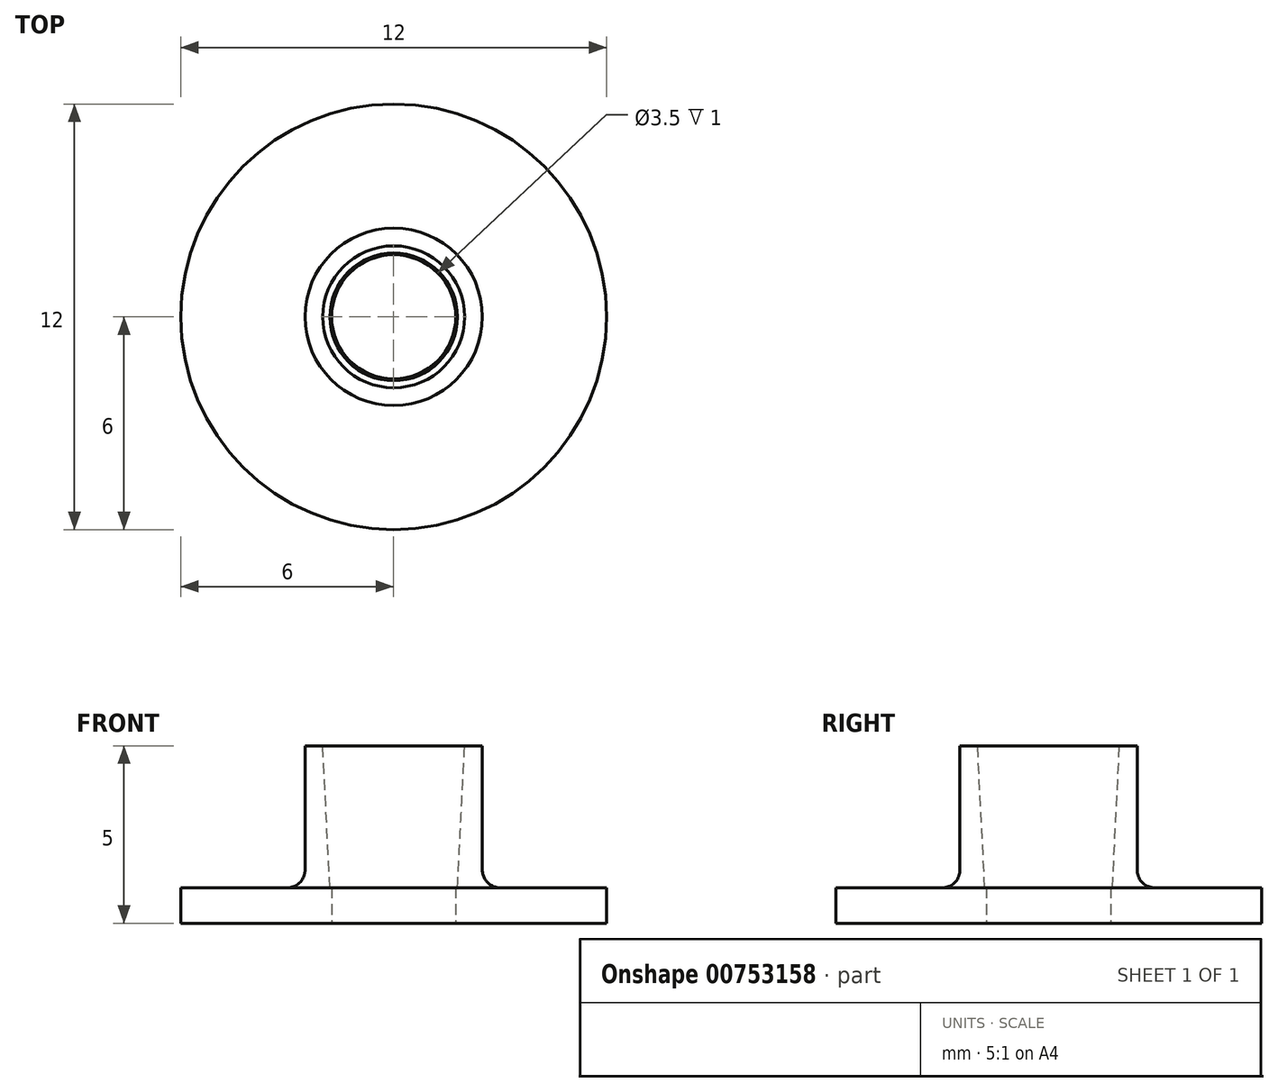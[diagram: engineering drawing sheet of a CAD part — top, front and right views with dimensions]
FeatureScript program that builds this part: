
annotation { "Feature Type Name" : "Feature", "Feature Type Description" : "" }
export const myFeature = defineFeature(function(context is Context, id is Id, definition is map)
    precondition{}
    {
        {
            var Q0;
            Q0=qCreatedBy(makeId("Top.planeOp"),FACE);
            var sketch = newSketch(context, id + "F0", { "sketchPlane" : qUnion([Q0])});
            skCircle(sketch, "E0", {"center": v(0, 0) * mm, "radius": 6 * mm});
            skCircle(sketch, "E1", {"center": v(0, 0) * mm, "radius": 1.75 * mm});
            skSolve(sketch);
        }
        {
            var Q0;
            Q0=qCreatedBy(makeId("Front.planeOp"),FACE);
            var sketch = newSketch(context, id + "F1", { "sketchPlane" : qUnion([Q0])});
            skLineSegment(sketch, "E2", {"start": v(0, 0) * mm, "end": v(0, 4) * mm});
            skSolve(sketch);
        }
        {
            var Q0;
            Q0=qCreatedBy(makeId("Front.planeOp"),FACE);
            var sketch = newSketch(context, id + "F2", { "sketchPlane" : qUnion([Q0])});
            skLineSegment(sketch, "E3", {"start": v(2.5, 0) * mm, "end": v(2.5, 5) * mm});
            skPoint(sketch, "E4.endSnap0", {"position": v(2.5, 2.5) * mm});
            skLineSegment(sketch, "E5", {"start": v(2.5, 0) * mm, "end": v(1.75, 0) * mm});
            skLineSegment(sketch, "E6", {"start": v(2.5, 5) * mm, "end": v(2, 5) * mm});
            skLineSegment(sketch, "E7", {"start": v(2, 5) * mm, "end": v(1.75, 0) * mm});
            skSolve(sketch);
        }
        {
            var Q0;
            Q0 = qSketchRegion(id + "F2", true);
            var Q1;
            Q1=sQuery(id+"F1.wireOp",EDGE,"E2");
            revolve(context, id + "F3", {"surfaceOperationType" : NewSurfaceOperationType.NEW, "entities" : qUnion([Q0]), "axis" : qUnion([Q1]), "revolveType" : RevolveType.FULL});
        }
        {
            var Q0;
            Q0 = qSketchRegion(id + "F0", true);
            extrude(context, id + "F4", {"entities" : qUnion([Q0]), "operationType" : NewBodyOperationType.ADD, "depth" : 1 * mm, "offsetDistance" : 25 * mm});
        }
        {
            var Q0;
            Q0=makeQuery(id+"F4.boolean.opBoolean","INTERSECT",EDGE,{"derivedFrom":[makeQuery(id+"F3.opRevolve","SWEPT_FACE",FACE,{"disambiguationData":[OSD([sQuery(id+"F2.wireOp",EDGE,"E3")])]}),makeQuery(id+"F4.opExtrude","CAP_FACE",FACE,{"disambiguationData":[OSD([sQuery(id+"F0.wireOp",EDGE,"E0"),sQuery(id+"F0.wireOp",EDGE,"E1")])],"isStart":false})]});
            fillet(context, id + "F5", {"entities" : qUnion([Q0]), "radius" : .5 * mm, "tangentPropagation" : true, "allowEdgeOverflow" : false});
        }
    });
